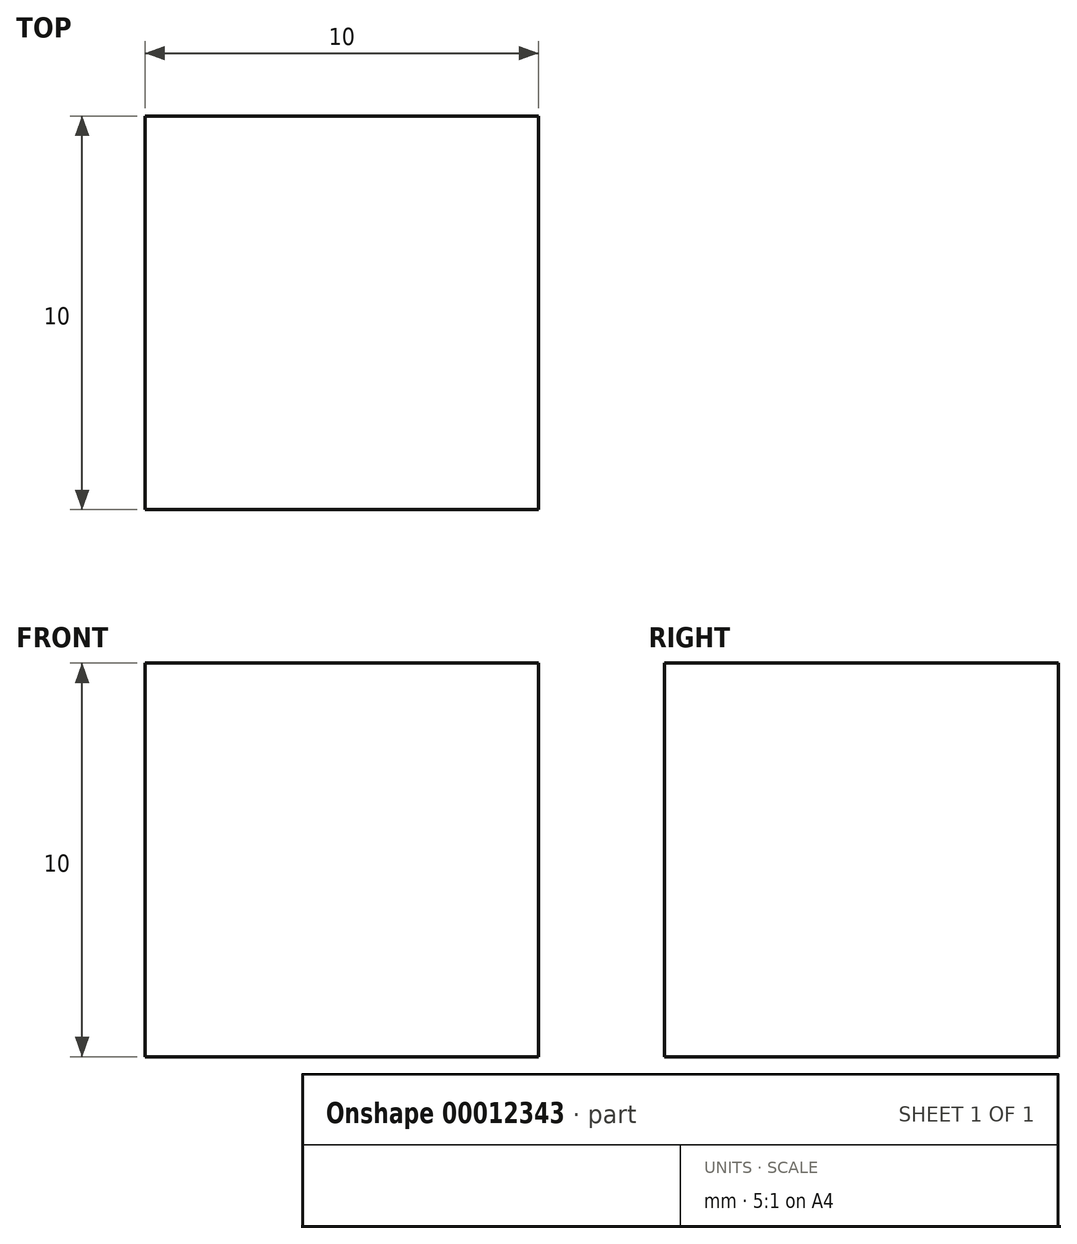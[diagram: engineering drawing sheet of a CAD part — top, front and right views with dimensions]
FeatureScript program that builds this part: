
annotation { "Feature Type Name" : "Feature", "Feature Type Description" : "" }
export const myFeature = defineFeature(function(context is Context, id is Id, definition is map)
    precondition{}
    {
        {
            var Q0;
            Q0=qCreatedBy(makeId("Top.planeOp"),FACE);
            var sketch = newSketch(context, id + "F0", { "sketchPlane" : qUnion([Q0])});
            skLineSegment(sketch, "E0.rect.bottom", {"start": v(-5, 5) * mm, "end": v(5, 5) * mm});
            skLineSegment(sketch, "E0.rect.top", {"start": v(-5, -5) * mm, "end": v(5, -5) * mm});
            skLineSegment(sketch, "E0.rect.left", {"start": v(-5, 5) * mm, "end": v(-5, -5) * mm});
            skLineSegment(sketch, "E0.rect.right", {"start": v(5, 5) * mm, "end": v(5, -5) * mm});
            skPoint(sketch, "E0.rect.middle", {"position": v(0, 0) * mm});
            skSolve(sketch);
        }
        {
            var Q0;
            Q0 = qSketchRegion(id + "F0", true);
            extrude(context, id + "F1", {"entities" : qUnion([Q0]), "depth" : 10 * mm});
        }
    });
